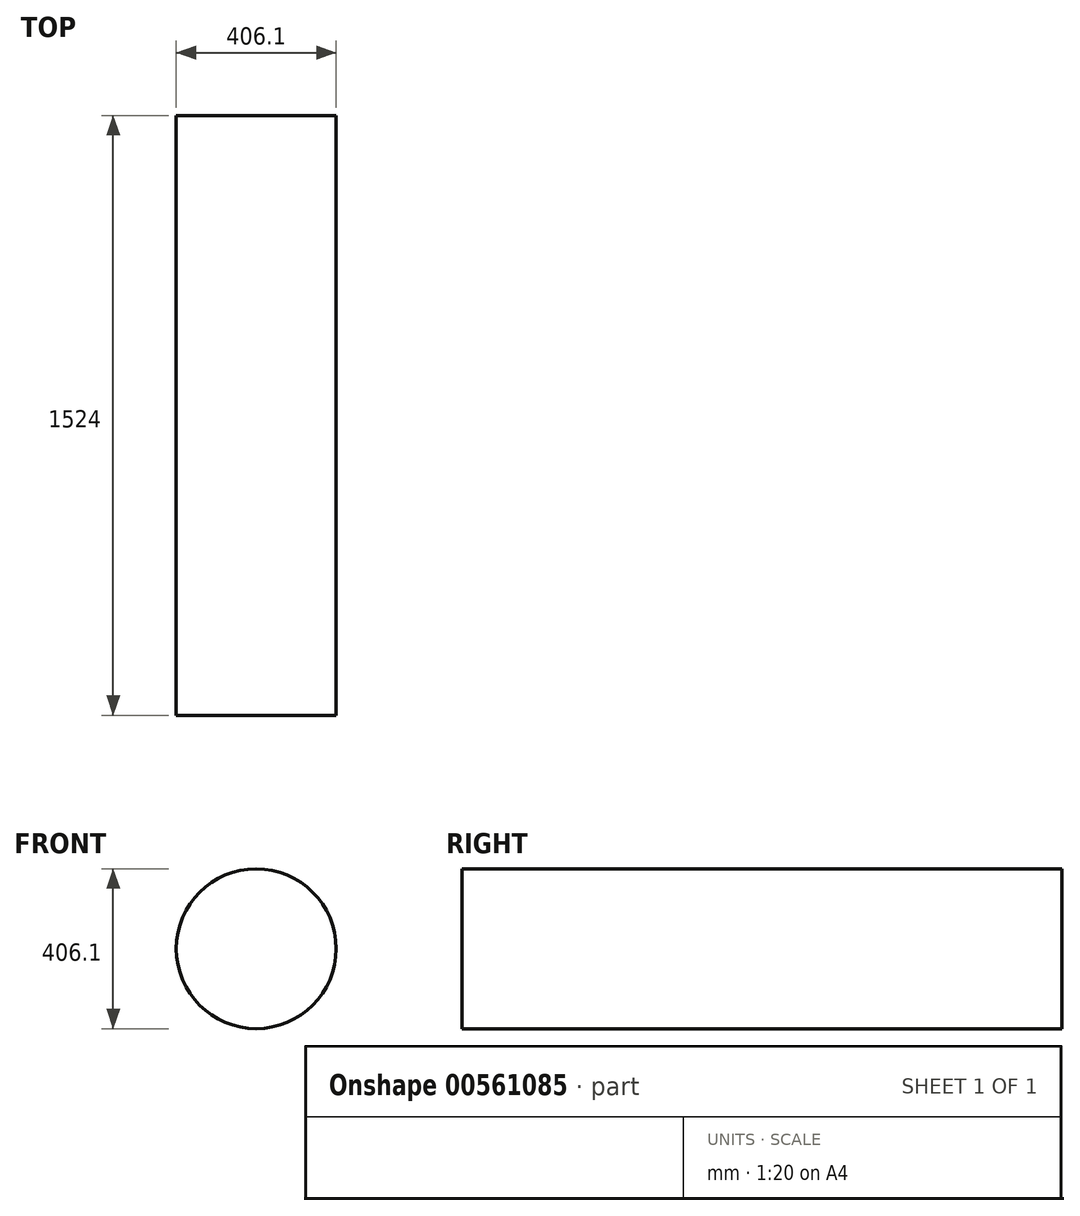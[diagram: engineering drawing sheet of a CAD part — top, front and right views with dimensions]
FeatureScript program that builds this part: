
annotation { "Feature Type Name" : "Feature", "Feature Type Description" : "" }
export const myFeature = defineFeature(function(context is Context, id is Id, definition is map)
    precondition{}
    {
        {
            var Q0;
            Q0=qCreatedBy(makeId("Front.planeOp"),FACE);
            var sketch = newSketch(context, id + "F0", { "sketchPlane" : qUnion([Q0])});
            skCircle(sketch, "E0", {"center": v(0, 0) * mm, "radius": 203.05 * mm});
            skSolve(sketch);
        }
        {
            var Q0;
            Q0=sQuery(id+"F0.wireOp",EDGE,"E0");
            extrude(context, id + "F1", {"bodyType" : ToolBodyType.SURFACE, "surfaceEntities" : qUnion([Q0]), "depth" : 1524 * mm, "offsetDistance" : 25.4 * mm});
        }
    });
